# Revit family: 1ad97cc6-7fdf-480a-b84c-ac1261f9478d
name_source: partatom
category: Plumbing Fixtures
revit_build: Autodesk Revit 2016 (Build: 20161004_0715(x64)
units: mm (PartAtom-declared; Revit-internal decimal feet)

## family parameters
Cut with Voids When Loaded = No
Host = Face
OmniClass Number = 23.45.55.11
OmniClass Title = Sanitary Components
Part Type = Normal
Room Calculation Point = No
Round Connector Dimension = Use Diameter
Shared = Yes

## types (1)
- FV600
    Assembly Code = C1030210
    CW Connection = No
    Cap Location from Back = 0' - 7 29/32"
    Cap Location from Top = 0' - 9 1/4"
    Cover Height = 2' - 3 13/16"
    Cover Height Control = 2' - 6 3/4"
    Cut to Height = Yes
    Default Elevation = 4' - 0"
    Depth = 0' - 10 9/16"
    Description = Ligature Resistant Flush Valve Cover
    Dimensional Note = The original height and depth of the Flush Valve Cover is 30.76" x 10.56"
    Finish = TPO-BSP-White
    HW Connection = No
    Height = 2' - 6 3/4"
    Manufacturer = Behavioral Safety Products
    Model = FV600
    Options = Includes Flush Valve Filler Patch
    Product Documentation Link = http://besafeprod.com
    Product Page URL = http://besafeprod.com
    Product data url = https://bimobject.com
    Show Filler Patch = Yes
    Type Image = <None>
    URL = http://besafeprod.com
    Vent Connection = No
    Waste Connection = No
    Width = 1' - 0 13/32"

## geometry (parser evidence)
native form markers: Blend x6, Sweep x6
no freeform markers — native parametric forms only
